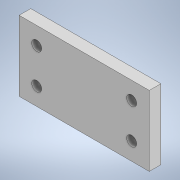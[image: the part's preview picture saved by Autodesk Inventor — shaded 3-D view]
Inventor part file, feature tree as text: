
AUTODESK INVENTOR PART (.ipt)
format: ipt  version: 2022 (Build 260153000, 153)  size: 107,520 bytes
history: native  units: mm
features: extrude x1, sketch x1
ambient origin geometry x8: Origin, YZ Plane, XZ Plane, XY Plane, X Axis, Y Axis, Z Axis, Center Point
bodies: Solid1 (feature_tree)
feature tree (2):
  extrude  "Extrusion1"  Depth=3.3mm
  sketch  "Sketch1"  dims[d24=9.95mm d27=9.95mm d31=5.0mm d32=5.0mm d33=5.0mm d34=5.0mm d35=3.3mm d36=0.0mm d40=5.0mm d41=5.0mm d42=5.0mm d43=27.0mm]
